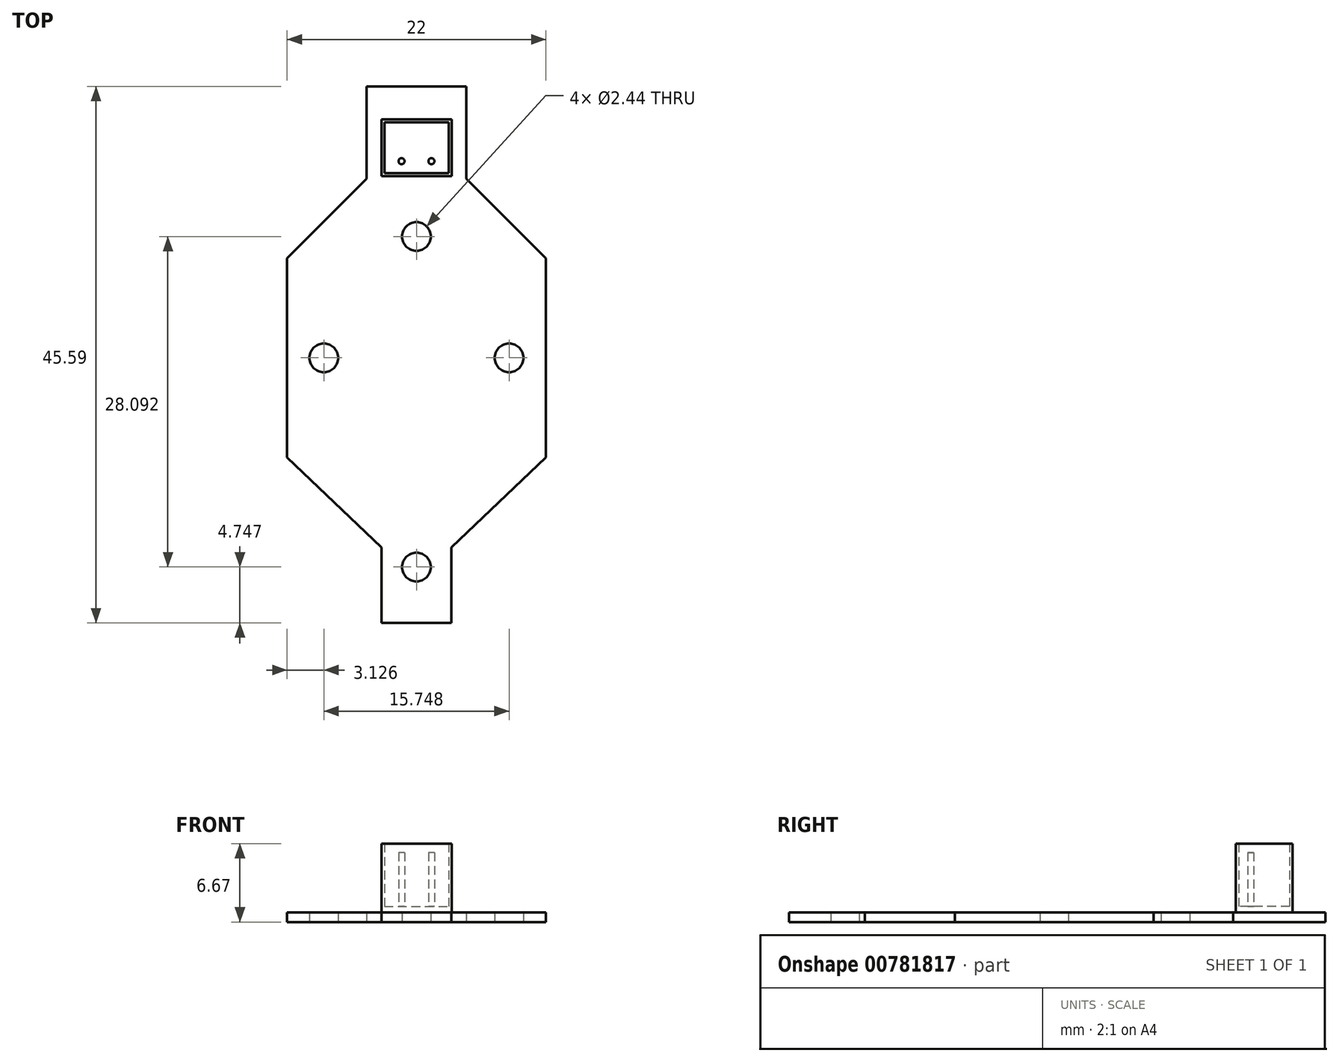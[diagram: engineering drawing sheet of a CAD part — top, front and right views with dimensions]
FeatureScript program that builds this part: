
annotation { "Feature Type Name" : "Feature", "Feature Type Description" : "" }
export const myFeature = defineFeature(function(context is Context, id is Id, definition is map)
    precondition{}
    {
        {
            var Q0;
            Q0=qCreatedBy(makeId("Top.planeOp"),FACE);
            var sketch = newSketch(context, id + "F0", { "sketchPlane" : qUnion([Q0])});
            skLineSegment(sketch, "E0", {"start": v(-4.24, 0) * mm, "end": v(4.24, 0) * mm});
            skLineSegment(sketch, "E1", {"start": v(4.24, 0) * mm, "end": v(4.24, -7.85) * mm});
            skLineSegment(sketch, "E2", {"start": v(4.24, -7.85) * mm, "end": v(11, -14.6) * mm});
            skLineSegment(sketch, "E3", {"start": v(11, -14.6) * mm, "end": v(11, -31.52) * mm});
            skLineSegment(sketch, "E4", {"start": v(11, -31.52) * mm, "end": v(2.97, -39.17) * mm});
            skLineSegment(sketch, "E5", {"start": v(2.97, -39.17) * mm, "end": v(2.97, -45.6) * mm});
            skLineSegment(sketch, "E6", {"start": v(2.97, -45.6) * mm, "end": v(-2.97, -45.6) * mm});
            skLineSegment(sketch, "E7", {"start": v(-2.97, -45.6) * mm, "end": v(-2.97, -39.17) * mm});
            skLineSegment(sketch, "E8", {"start": v(0, 5.78) * mm, "end": v(0, -68.9) * mm, "construction": true});
            skPoint(sketch, "E9", {"position": v(0, 0) * mm});
            skPoint(sketch, "E10", {"position": v(0, -45.6) * mm});
            skLineSegment(sketch, "E11", {"start": v(-2.97, -39.17) * mm, "end": v(-11, -31.52) * mm});
            skLineSegment(sketch, "E12", {"start": v(-11, -31.52) * mm, "end": v(-11, -14.6) * mm});
            skLineSegment(sketch, "E13", {"start": v(-11, -14.6) * mm, "end": v(-4.24, -7.85) * mm});
            skLineSegment(sketch, "E14", {"start": v(-4.24, -7.85) * mm, "end": v(-4.24, 0) * mm});
            skCircle(sketch, "E15", {"center": v(0, -12.75) * mm, "radius": 1.22 * mm});
            skCircle(sketch, "E16", {"center": v(7.87, -23.06) * mm, "radius": 1.22 * mm});
            skCircle(sketch, "E17", {"center": v(-7.87, -23.06) * mm, "radius": 1.22 * mm});
            skCircle(sketch, "E18", {"center": v(0, -40.84) * mm, "radius": 1.22 * mm});
            skLineSegment(sketch, "E19", {"start": v(-11, -23.06) * mm, "end": v(11, -23.06) * mm, "construction": true});
            skLineSegment(sketch, "E20", {"start": v(-7.87, -23.06) * mm, "end": v(7.87, -23.06) * mm, "construction": true});
            skPoint(sketch, "E21", {"position": v(0, -23.06) * mm});
            skSolve(sketch);
        }
        {
            var Q0;
            Q0=makeQuery(id+"F0.imprint","IMPRINT",FACE,{"disambiguationData":[TD([[makeQuery(id+"F0.imprint","IMPRINT",EDGE,{"derivedFrom":sQuery(id+"F0.wireOp",EDGE,"E0")}),-1.0]])]});
            extrude(context, id + "F1", {"entities" : qUnion([Q0]), "depth" : 0.83 * mm, "offsetDistance" : 25.4 * mm});
        }
        {
            var Q0;
            Q0=makeQuery(id+"F1.opExtrude","CAP_FACE",FACE,{"disambiguationData":[OSD([sQuery(id+"F0.wireOp",EDGE,"E0"),sQuery(id+"F0.wireOp",EDGE,"E1"),sQuery(id+"F0.wireOp",EDGE,"E2"),sQuery(id+"F0.wireOp",EDGE,"E3"),sQuery(id+"F0.wireOp",EDGE,"E4"),sQuery(id+"F0.wireOp",EDGE,"E5"),sQuery(id+"F0.wireOp",EDGE,"E6"),sQuery(id+"F0.wireOp",EDGE,"E7"),sQuery(id+"F0.wireOp",EDGE,"E11"),sQuery(id+"F0.wireOp",EDGE,"E12"),sQuery(id+"F0.wireOp",EDGE,"E13"),sQuery(id+"F0.wireOp",EDGE,"E14"),sQuery(id+"F0.wireOp",EDGE,"E15"),sQuery(id+"F0.wireOp",EDGE,"E16"),sQuery(id+"F0.wireOp",EDGE,"E17"),sQuery(id+"F0.wireOp",EDGE,"E18")])],"isStart":false});
            var sketch = newSketch(context, id + "F2", { "sketchPlane" : qUnion([Q0])});
            skLineSegment(sketch, "E22.bottom", {"start": v(-2.98, -2.8) * mm, "end": v(2.98, -2.8) * mm});
            skLineSegment(sketch, "E22.top", {"start": v(-2.98, -7.62) * mm, "end": v(2.98, -7.62) * mm});
            skLineSegment(sketch, "E22.left", {"start": v(-2.98, -2.8) * mm, "end": v(-2.98, -7.62) * mm});
            skLineSegment(sketch, "E22.right", {"start": v(2.98, -2.8) * mm, "end": v(2.98, -7.62) * mm});
            skPoint(sketch, "E23", {"position": v(0, -2.8) * mm});
            skLineSegment(sketch, "E24.bottom", {"start": v(-2.73, -3.05) * mm, "end": v(2.73, -3.05) * mm});
            skLineSegment(sketch, "E24.top", {"start": v(-2.73, -7.37) * mm, "end": v(2.73, -7.37) * mm});
            skLineSegment(sketch, "E24.left", {"start": v(-2.73, -3.05) * mm, "end": v(-2.73, -7.37) * mm});
            skLineSegment(sketch, "E24.right", {"start": v(2.73, -3.05) * mm, "end": v(2.73, -7.37) * mm});
            skCircle(sketch, "E25", {"center": v(-1.27, -6.35) * mm, "radius": 0.25 * mm});
            skCircle(sketch, "E26", {"center": v(1.27, -6.35) * mm, "radius": 0.25 * mm});
            skLineSegment(sketch, "E27", {"start": v(-1.27, -6.35) * mm, "end": v(1.27, -6.35) * mm, "construction": true});
            skPoint(sketch, "E28", {"position": v(0, -6.35) * mm});
            skSolve(sketch);
        }
        {
            var Q0;
            Q0=makeQuery(id+"F2.imprint","IMPRINT",FACE,{"disambiguationData":[TD([[makeQuery(id+"F2.imprint","IMPRINT",EDGE,{"derivedFrom":sQuery(id+"F2.wireOp",EDGE,"E22.bottom")}),-1.0]])]});
            extrude(context, id + "F3", {"entities" : qUnion([Q0]), "operationType" : NewBodyOperationType.ADD, "depth" : 5.84 * mm, "offsetDistance" : 25.4 * mm});
        }
        {
            var Q0;
            Q0=makeQuery(id+"F2.imprint","IMPRINT",FACE,{"disambiguationData":[TD([[makeQuery(id+"F2.imprint","IMPRINT",EDGE,{"derivedFrom":sQuery(id+"F2.wireOp",EDGE,"E24.bottom")}),-1.0]])]});
            extrude(context, id + "F4", {"entities" : qUnion([Q0]), "operationType" : NewBodyOperationType.ADD, "depth" : 0.5 * mm, "offsetDistance" : 25.4 * mm});
        }
        {
            var Q0;
            Q0=makeQuery(id+"F2.imprint","IMPRINT",FACE,{"disambiguationData":[TD([[makeQuery(id+"F2.imprint","IMPRINT",EDGE,{"derivedFrom":sQuery(id+"F2.wireOp",EDGE,"E25")}),1.0]])]});
            var Q1;
            Q1=makeQuery(id+"F2.imprint","IMPRINT",FACE,{"disambiguationData":[TD([[makeQuery(id+"F2.imprint","IMPRINT",EDGE,{"derivedFrom":sQuery(id+"F2.wireOp",EDGE,"E26")}),1.0]])]});
            extrude(context, id + "F5", {"entities" : qUnion([Q0, Q1]), "operationType" : NewBodyOperationType.ADD, "depth" : 5.08 * mm, "offsetDistance" : 25.4 * mm});
        }
    });
